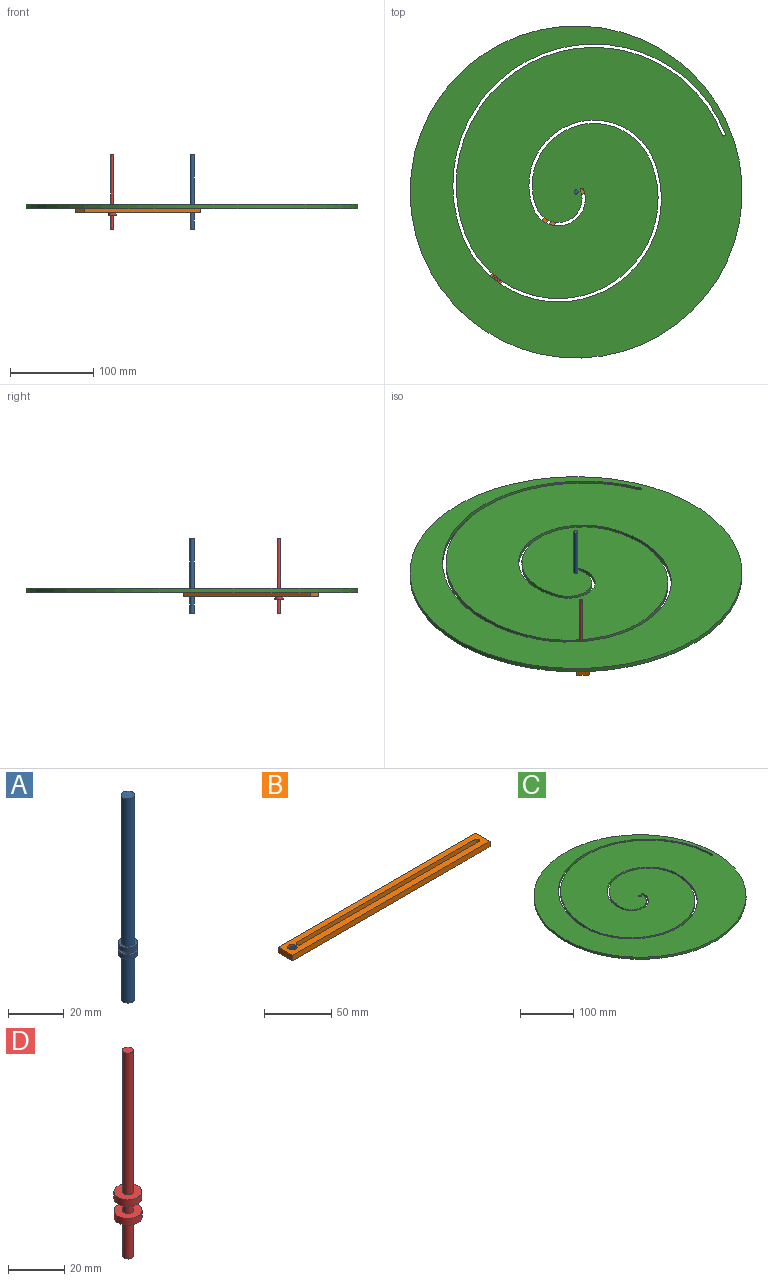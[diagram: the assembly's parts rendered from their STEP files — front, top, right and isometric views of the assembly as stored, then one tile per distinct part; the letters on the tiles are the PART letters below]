
ASSEMBLY  parts=4 mates=3
PART A: 11 faces, bbox 7x7x90 mm
  f0: cylinder r=2.5mm len=5mm, axis (0,0,-1), area 18.8mm2, adj f2,f7
  f1: cylinder r=3.5mm len=7mm, axis (0,0,1), area 41.8mm2, adj f2,f3
  f2: plane 7x7mm, normal (0,0,-1), area 18.8mm2, adj f0,f1
  f3: plane 7x7mm, normal (0,0,1), area 18.8mm2, adj f1,f5
  f4: plane 5x5mm, normal (0,0,1), area 19.6mm2, adj f5
  f5: cylinder r=2.5mm len=65mm, axis (0,0,-1), area 1021mm2, adj f3,f4
  f6: cylinder r=3.5mm len=7mm, axis (0,0,-1), area 41.8mm2, adj f7,f8
  f7: plane 7x7mm, normal (0,0,1), area 18.8mm2, adj f0,f6
  f8: plane 7x7mm, normal (0,0,-1), area 18.8mm2, adj f6,f10
  f9: plane 5x5mm, normal (0,0,-1), area 19.6mm2, adj f10
  f10: cylinder r=2.5mm len=20mm, axis (0,0,-1), area 314.2mm2, adj f8,f9
PART B: 15 faces, bbox 207.5x15x5 mm
  f0: cylinder r=2.75mm len=5.5mm, axis (0,0,-1), area 17.3mm2, adj f12,f14
  f1: plane 207.5x5mm, normal (0,1,0), area 1037.5mm2, adj f2,f8,f9,f10
  f2: plane 15x5mm, normal (-1,0,0), area 75mm2, adj f1,f3,f9,f10
  f3: plane 207.5x5mm, normal (0,-1,0), area 1037.5mm2, adj f2,f8,f9,f10
  f4: cylinder r=2mm len=5mm, axis (0,0,-1), area 31.4mm2, adj f5,f7,f9,f10
  f5: plane 187x5mm, normal (0,1,0), area 935mm2, adj f4,f6,f9,f10
  f6: cylinder r=2mm len=5mm, axis (0,0,-1), area 31.4mm2, adj f5,f7,f9,f10
  f7: plane 187x5mm, normal (0,-1,0), area 935mm2, adj f4,f6,f9,f10
  f8: plane 15x5mm, normal (1,0,0), area 75mm2, adj f1,f3,f9,f10
  f9: plane 207.5x15mm, normal (0,0,1), area 2313.4mm2, adj f1,f2,f3,f4,f5,f6,f7,f8
  f10: plane 207.5x15mm, normal (0,0,-1), area 2313.4mm2, adj f1,f2,f3,f4,f5,f6,f7,f8
  f11: cylinder r=3.5mm len=7mm, axis (0,0,1), area 44mm2, adj f9,f12
  f12: plane 7x7mm, normal (0,0,1), area 14.7mm2, adj f0,f11
  f13: cylinder r=3.5mm len=7mm, axis (0,0,-1), area 44mm2, adj f10,f14
  f14: plane 7x7mm, normal (0,0,-1), area 14.7mm2, adj f0,f13
PART C: 14 faces, bbox 400x400x5 mm
  f0: cylinder r=32.41mm len=64.81mm, axis (0,0,-1), area 509mm2, adj f1,f9,f11,f12
  f1: cylinder r=2mm len=5mm, axis (0,0,-1), area 31.8mm2, adj f0,f2,f11,f12
  f2: cylinder r=28.41mm len=56.81mm, axis (0,0,-1), area 446.2mm2, adj f1,f3,f11,f12
  f3: cylinder r=74.22mm len=148.44mm, axis (0,0,-1), area 1165.8mm2, adj f2,f4,f11,f12
  f4: cylinder r=120.03mm len=240.06mm, axis (0,0,-1), area 1885.4mm2, adj f3,f5,f11,f12
  f5: cylinder r=165.84mm len=331.69mm, axis (0,0,-1), area 2605.1mm2, adj f4,f6,f11,f12
  f6: cylinder r=2mm len=5mm, axis (0,0,-1), area 31.2mm2, adj f5,f7,f11,f12
  f7: cylinder r=169.84mm len=339.69mm, axis (0,0,-1), area 2667.9mm2, adj f6,f8,f11,f12
  f8: cylinder r=124.03mm len=248.06mm, axis (0,0,-1), area 1948.3mm2, adj f7,f9,f11,f12
  f9: cylinder r=78.22mm len=156.44mm, axis (0,0,-1), area 1228.7mm2, adj f0,f8,f11,f12
  f10: cylinder r=200mm len=400mm, axis (0,0,-1), area 6283.2mm2, adj f11,f12
  f11: plane 400x400mm, normal (0,0,1), area 120648.9mm2, adj f0,f1,f2,f3,f4,f5,f6,f7
  f12: plane 400x400mm, normal (0,0,-1), area 120648.9mm2, adj f0,f1,f2,f3,f4,f5,f6,f7
  f13: cylinder r=2.5mm len=5mm, axis (0,0,1), area 78.5mm2, adj f11,f12
PART D: 11 faces, bbox 10x10x89.9 mm
  f0: cylinder r=1.95mm len=5.2mm, axis (0,0,1), area 63.7mm2, adj f3,f6
  f1: cylinder r=5mm len=10mm, axis (0,0,-1), area 94.2mm2, adj f2,f3
  f2: plane 10x10mm, normal (0,0,1), area 66.6mm2, adj f1,f7
  f3: plane 10x10mm, normal (0,0,-1), area 66.6mm2, adj f0,f1
  f4: cylinder r=5mm len=10mm, axis (0,0,1), area 94.2mm2, adj f5,f6
  f5: plane 10x10mm, normal (0,0,-1), area 66.6mm2, adj f4,f9
  f6: plane 10x10mm, normal (0,0,1), area 66.6mm2, adj f0,f4
  f7: cylinder r=1.95mm len=61.8mm, axis (0,0,-1), area 757.2mm2, adj f2,f8
  f8: plane 3.9x3.9mm, normal (0,0,1), area 11.9mm2, adj f7
  f9: cylinder r=1.95mm len=16.9mm, axis (0,0,1), area 207.1mm2, adj f5,f10
  f10: plane 3.9x3.9mm, normal (0,0,-1), area 11.9mm2, adj f9
PLACE A rot(axis=(0,0,1),21.3deg) t=(24.31,48.72,-47.77)mm fixed
PLACE B rot(axis=(0,0,-1),132.5deg) t=(24.31,48.72,-47.77)mm
PLACE C rot(axis=(0,0,1),21.3deg) t=(24.31,48.72,-12.77)mm
PLACE D rot(axis=(0,0,-1),42.1deg) t=(-83.04,-45.86,-47.87)mm
MATE slider C.f13 <-> A.f0  axis (0,0,1) through (24.31,48.72,-37.77)mm
MATE planar D.f0 <-> B.f9  axis (0,0,-1) through (-71.86,-55.94,-42.77)mm
MATE revolute B.f11 <-> A.f1  axis (0,0,1) through (24.31,48.72,-42.77)mm
